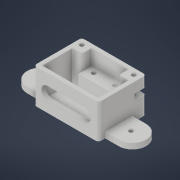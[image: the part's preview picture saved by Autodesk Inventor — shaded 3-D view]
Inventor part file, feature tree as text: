
AUTODESK INVENTOR PART (.ipt)
format: ipt  version: 2022 (Build 260153000, 153)  size: 275,968 bytes
history: native  units: mm
features: extrude x10, sketch x10, fillet x3, other x1, shell x1
ambient origin geometry x8: Origin, YZ Plane, XZ Plane, XY Plane, X Axis, Y Axis, Z Axis, Center Point
bodies: Body1 (feature_tree)
feature tree (25):
  other  "Sólido1"
  extrude  "Extrusão1"  Depth=35.0mm
  shell  "Casca1"  Thickness=25.0mm
  extrude  "Extrusão2"  Depth=9.3mm
  extrude  "Extrusão3"  Depth=9.3mm
  sketch  "Esboço4"  dims[d10=20.0mm d11=0.0mm d12=7.0mm]
  fillet  "Arredondamento1"  Radius=27.0mm
  fillet  "Arredondamento2"  Radius=10.0mm
  extrude  "Extrusão26"  Depth=7.0mm
  extrude  "Extrusão28"  Depth=7.0mm
  fillet  "Arredondamento9"  Radius=7.0mm
  extrude  "Extrusão29"  Depth=26.0mm
  extrude  "Extrusão32"  Depth=0.5mm
  extrude  "Extrusão33"  Depth=2.0mm
  extrude  "Extrusão34"  Depth=4.0mm
  extrude  "Extrusion40"  Depth=20.0mm TaperAngle=0.0deg
  sketch  "Esboço1"  dims[d0=47.0mm d1=35.0mm d2=25.0mm d3=0.0mm]
  sketch  "Esboço2"  dims[d4=3.0mm d5=9.3mm]
  sketch  "Esboço3"  dims[d6=12.5mm d7=9.3mm d8=27.0mm d9=10.0mm]
  sketch  "Esboço35"  dims[d13=7.0mm d14=7.0mm d15=7.0mm]
  sketch  "Esboço37"  dims[d20=22.0mm d21=0.0mm d33=26.0mm]
  sketch  "Esboço38"  dims[d34=10.0mm d35=0.5mm]
  sketch  "Esboço40"  dims[d63=2.0mm d64=2.0mm]
  sketch  "Esboço42"  dims[d160=20.0mm d161=4.0mm]
  sketch  "Esboço44"  dims[d162=5.0mm d163=20.0mm d164=0.0mm d170=20.0mm d171=0.0mm d172=10.0mm d173=3.0mm d174=3.0mm d175=3.0mm d176=10.0mm d177=9.0mm d178=10.0mm d179=9.0mm d180=10.0mm d181=9.0mm d182=20.0mm d183=0.0mm d222=8.5mm d223=5.0mm d224=8.5mm d225=0.0mm d226=3.01mm d227=4.5mm d228=4.5mm d229=20.0mm d231=26.0mm d232=20.0mm d234=38.0mm d237=20.0mm d238=0.0mm d239=8.5mm d240=5.0mm d241=7.5mm d242=7.5mm d243=8.5mm d244=0.0mm d271=3.0mm d272=3.0mm d273=11.0mm d274=0.0mm]
